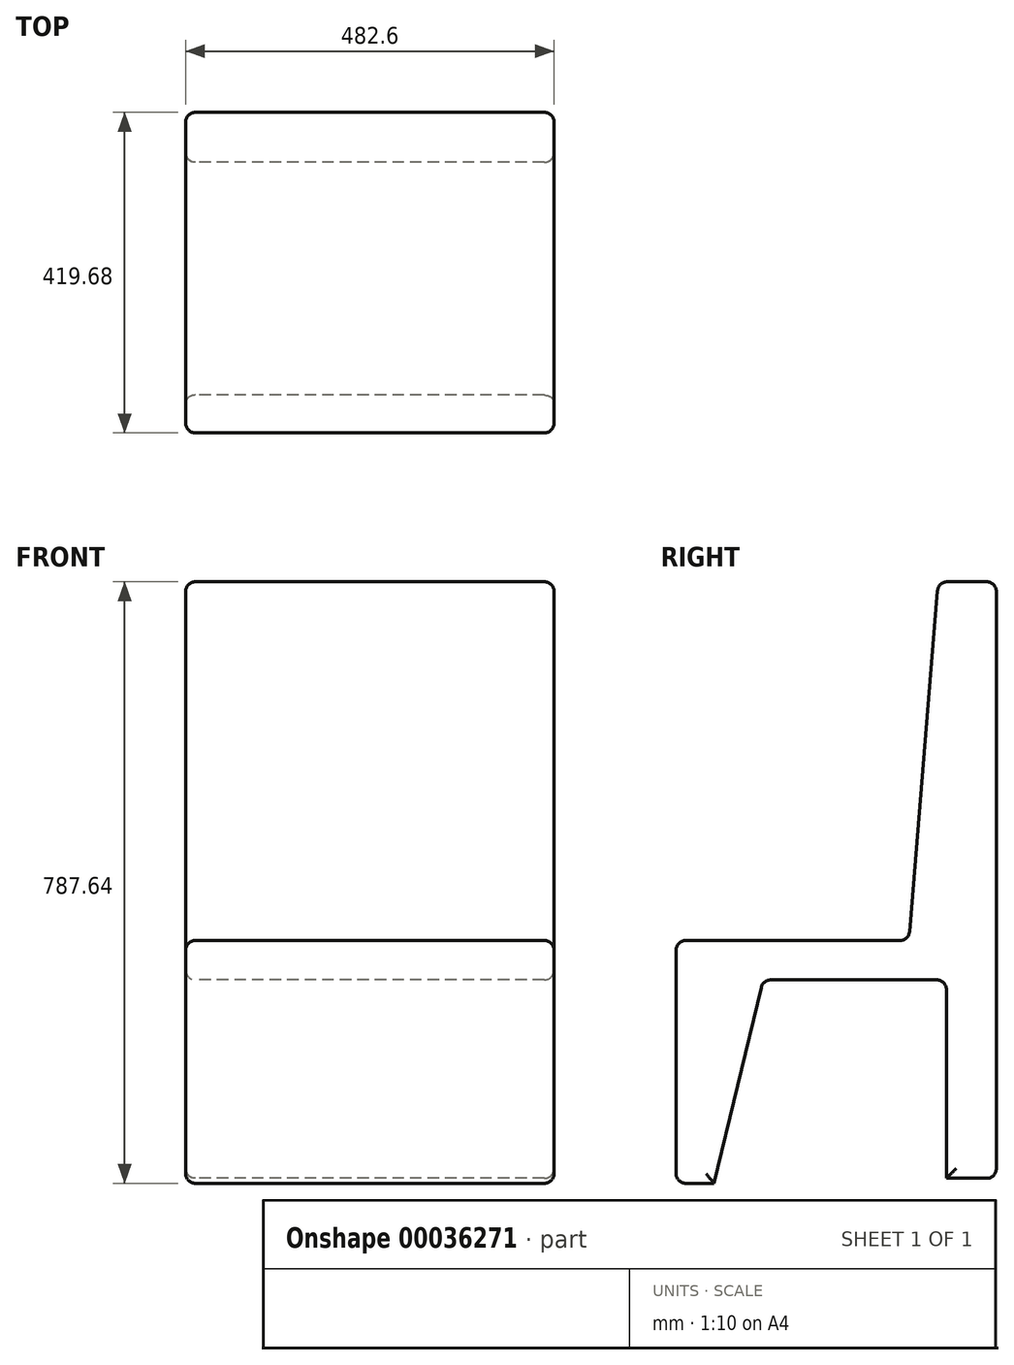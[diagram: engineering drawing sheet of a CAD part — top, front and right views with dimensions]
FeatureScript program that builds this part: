
annotation { "Feature Type Name" : "Feature", "Feature Type Description" : "" }
export const myFeature = defineFeature(function(context is Context, id is Id, definition is map)
    precondition{}
    {
        {
            var Q0;
            Q0=qCreatedBy(makeId("Right.planeOp"),FACE);
            var sketch = newSketch(context, id + "F0", { "sketchPlane" : qUnion([Q0])});
            skLineSegment(sketch, "E0", {"start": v(-42.47, 69.38) * mm, "end": v(33.73, 69.38) * mm});
            skLineSegment(sketch, "E1", {"start": v(33.73, 69.38) * mm, "end": v(33.73, -718.02) * mm});
            skLineSegment(sketch, "E2", {"start": v(-42.47, 69.38) * mm, "end": v(-81, -400.42) * mm});
            skLineSegment(sketch, "E3", {"start": v(-81, -400.42) * mm, "end": v(-385.95, -400.42) * mm});
            skLineSegment(sketch, "E4", {"start": v(-385.95, -400.42) * mm, "end": v(-385.95, -718.26) * mm});
            skLineSegment(sketch, "E5", {"start": v(-385.95, -718.26) * mm, "end": v(-336.56, -718.26) * mm});
            skLineSegment(sketch, "E6", {"start": v(-336.56, -718.26) * mm, "end": v(-272.13, -451.96) * mm});
            skLineSegment(sketch, "E7", {"start": v(-272.13, -451.96) * mm, "end": v(-31.76, -451.96) * mm});
            skLineSegment(sketch, "E8", {"start": v(-31.76, -451.96) * mm, "end": v(-31.76, -711.82) * mm});
            skLineSegment(sketch, "E9", {"start": v(-31.76, -711.82) * mm, "end": v(33.73, -711.82) * mm});
            skSolve(sketch);
        }
        {
            var Q0;
            {var subQ2=sQuery(id+"F0.wireOp",EDGE,"E0");Q0=makeQuery(id+"F0.imprint","IMPRINT",FACE,{"disambiguationData":[TD([[makeQuery(id+"F0.imprint","IMPRINT",EDGE,{"derivedFrom":subQ2}),-1.0]])]});}
            extrude(context, id + "F1", {"entities" : qUnion([Q0]), "depth" : 482.6 * mm});
        }
        {
            var Q0;
            Q0=makeQuery(id+"F1.opExtrude","SWEPT_FACE",FACE,{"disambiguationData":[OSD([sQuery(id+"F0.wireOp",EDGE,"E4")])]});
            var Q1;
            Q1=makeQuery(id+"F1.opExtrude","SWEPT_FACE",FACE,{"disambiguationData":[OSD([sQuery(id+"F0.wireOp",EDGE,"E3")])]});
            var Q2;
            Q2=makeQuery(id+"F1.opExtrude","CAP_FACE",FACE,{"disambiguationData":[OSD([sQuery(id+"F0.wireOp",EDGE,"E0"),sQuery(id+"F0.wireOp",EDGE,"E1"),sQuery(id+"F0.wireOp",EDGE,"E2"),sQuery(id+"F0.wireOp",EDGE,"E3"),sQuery(id+"F0.wireOp",EDGE,"E4"),sQuery(id+"F0.wireOp",EDGE,"E5"),sQuery(id+"F0.wireOp",EDGE,"E6"),sQuery(id+"F0.wireOp",EDGE,"E7"),sQuery(id+"F0.wireOp",EDGE,"E8"),sQuery(id+"F0.wireOp",EDGE,"E9")])],"isStart":false});
            var Q3;
            Q3=makeQuery(id+"F1.opExtrude","SWEPT_FACE",FACE,{"disambiguationData":[OSD([sQuery(id+"F0.wireOp",EDGE,"E2")])]});
            var Q4;
            Q4=makeQuery(id+"F1.opExtrude","SWEPT_FACE",FACE,{"disambiguationData":[OSD([sQuery(id+"F0.wireOp",EDGE,"E0")])]});
            var Q5;
            Q5=makeQuery(id+"F1.opExtrude","SWEPT_FACE",FACE,{"disambiguationData":[OSD([sQuery(id+"F0.wireOp",EDGE,"E1")])]});
            var Q6;
            Q6=makeQuery(id+"F1.opExtrude","CAP_FACE",FACE,{"disambiguationData":[OSD([sQuery(id+"F0.wireOp",EDGE,"E0"),sQuery(id+"F0.wireOp",EDGE,"E1"),sQuery(id+"F0.wireOp",EDGE,"E2"),sQuery(id+"F0.wireOp",EDGE,"E3"),sQuery(id+"F0.wireOp",EDGE,"E4"),sQuery(id+"F0.wireOp",EDGE,"E5"),sQuery(id+"F0.wireOp",EDGE,"E6"),sQuery(id+"F0.wireOp",EDGE,"E7"),sQuery(id+"F0.wireOp",EDGE,"E8"),sQuery(id+"F0.wireOp",EDGE,"E9")])],"isStart":true});
            var Q7;
            Q7=makeQuery(id+"F1.opExtrude","CAP_EDGE",EDGE,{"disambiguationData":[OSD([sQuery(id+"F0.wireOp",EDGE,"E2")])],"isStart":true});
            var Q8;
            Q8=makeQuery(id+"F1.opExtrude","SWEPT_EDGE",EDGE,{"disambiguationData":[OSD([sQuery(id+"F0.wireOp",EDGE,"E0"),sQuery(id+"F0.wireOp",EDGE,"E2")])]});
            var Q9;
            Q9=makeQuery(id+"F1.opExtrude","SWEPT_EDGE",EDGE,{"disambiguationData":[OSD([sQuery(id+"F0.wireOp",EDGE,"E0"),sQuery(id+"F0.wireOp",EDGE,"E1")])]});
            var Q10;
            Q10=makeQuery(id+"F1.opExtrude","CAP_EDGE",EDGE,{"disambiguationData":[OSD([sQuery(id+"F0.wireOp",EDGE,"E8")])],"isStart":true});
            var Q11;
            Q11=makeQuery(id+"F1.opExtrude","SWEPT_EDGE",EDGE,{"disambiguationData":[OSD([sQuery(id+"F0.wireOp",EDGE,"E3"),sQuery(id+"F0.wireOp",EDGE,"E4")])]});
            var Q12;
            Q12=makeQuery(id+"F1.opExtrude","CAP_EDGE",EDGE,{"disambiguationData":[OSD([sQuery(id+"F0.wireOp",EDGE,"E7")])],"isStart":true});
            var Q13;
            Q13=makeQuery(id+"F1.opExtrude","CAP_EDGE",EDGE,{"disambiguationData":[OSD([sQuery(id+"F0.wireOp",EDGE,"E1")])],"isStart":true});
            var Q14;
            Q14=makeQuery(id+"F1.opExtrude","CAP_EDGE",EDGE,{"disambiguationData":[OSD([sQuery(id+"F0.wireOp",EDGE,"E3")])],"isStart":true});
            var Q15;
            Q15=makeQuery(id+"F1.opExtrude","CAP_EDGE",EDGE,{"disambiguationData":[OSD([sQuery(id+"F0.wireOp",EDGE,"E2")])],"isStart":false});
            var Q16;
            Q16=makeQuery(id+"F1.opExtrude","SWEPT_EDGE",EDGE,{"disambiguationData":[OSD([sQuery(id+"F0.wireOp",EDGE,"E2"),sQuery(id+"F0.wireOp",EDGE,"E3")])]});
            var Q17;
            Q17=makeQuery(id+"F1.opExtrude","CAP_EDGE",EDGE,{"disambiguationData":[OSD([sQuery(id+"F0.wireOp",EDGE,"E7")])],"isStart":false});
            var Q18;
            Q18=makeQuery(id+"F1.opExtrude","CAP_EDGE",EDGE,{"disambiguationData":[OSD([sQuery(id+"F0.wireOp",EDGE,"E6")])],"isStart":false});
            var Q19;
            Q19=makeQuery(id+"F1.opExtrude","SWEPT_EDGE",EDGE,{"disambiguationData":[OSD([sQuery(id+"F0.wireOp",EDGE,"E6"),sQuery(id+"F0.wireOp",EDGE,"E7")])]});
            var Q20;
            Q20=makeQuery(id+"F1.opExtrude","CAP_EDGE",EDGE,{"disambiguationData":[OSD([sQuery(id+"F0.wireOp",EDGE,"E6")])],"isStart":true});
            var Q21;
            Q21=makeQuery(id+"F1.opExtrude","SWEPT_EDGE",EDGE,{"disambiguationData":[OSD([sQuery(id+"F0.wireOp",EDGE,"E7"),sQuery(id+"F0.wireOp",EDGE,"E8")])]});
            var Q22;
            Q22=makeQuery(id+"F1.opExtrude","CAP_EDGE",EDGE,{"disambiguationData":[OSD([sQuery(id+"F0.wireOp",EDGE,"E4")])],"isStart":false});
            var Q23;
            Q23=makeQuery(id+"F1.opExtrude","CAP_EDGE",EDGE,{"disambiguationData":[OSD([sQuery(id+"F0.wireOp",EDGE,"E0")])],"isStart":true});
            var Q24;
            Q24=makeQuery(id+"F1.opExtrude","CAP_EDGE",EDGE,{"disambiguationData":[OSD([sQuery(id+"F0.wireOp",EDGE,"E3")])],"isStart":false});
            fillet(context, id + "F2", {"entities" : qUnion([Q0, Q1, Q2, Q3, Q4, Q5, Q6, Q7, Q8, Q9, Q10, Q11, Q12, Q13, Q14, Q15, Q16, Q17, Q18, Q19, Q20, Q21, Q22, Q23, Q24]), "radius" : 12.7 * mm, "tangentPropagation" : true, "allowEdgeOverflow" : false});
        }
    });
